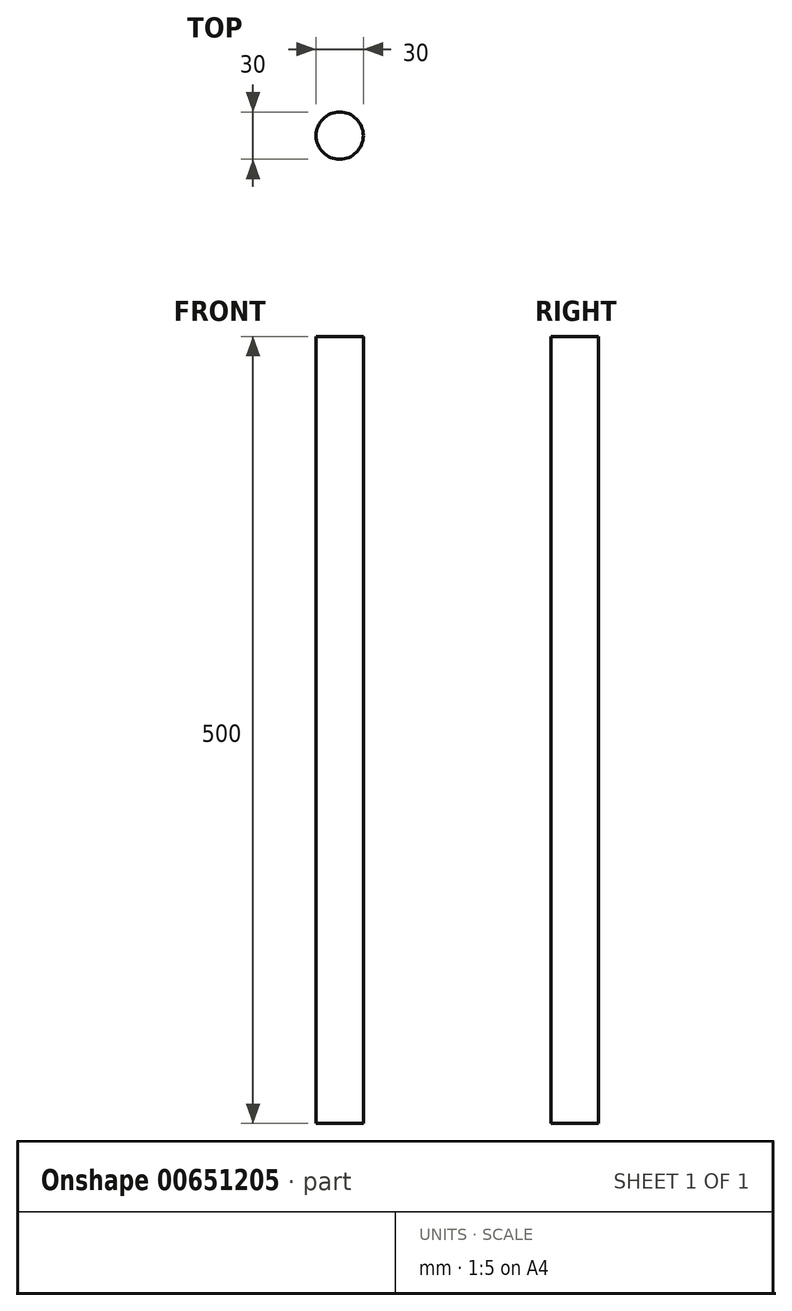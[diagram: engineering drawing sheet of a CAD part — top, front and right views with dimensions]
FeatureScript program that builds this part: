
annotation { "Feature Type Name" : "Feature", "Feature Type Description" : "" }
export const myFeature = defineFeature(function(context is Context, id is Id, definition is map)
    precondition{}
    {
        {
            var Q0;
            Q0=qCreatedBy(makeId("Top.planeOp"),FACE);
            var sketch = newSketch(context, id + "F0", { "sketchPlane" : qUnion([Q0])});
            skCircle(sketch, "E0", {"center": v(0, 0) * mm, "radius": 15 * mm});
            skSolve(sketch);
        }
        {
            var Q0;
            Q0 = qSketchRegion(id + "F0", true);
            extrude(context, id + "F1", {"entities" : qUnion([Q0]), "depth" : 500 * mm, "offsetDistance" : 25 * mm});
        }
    });
